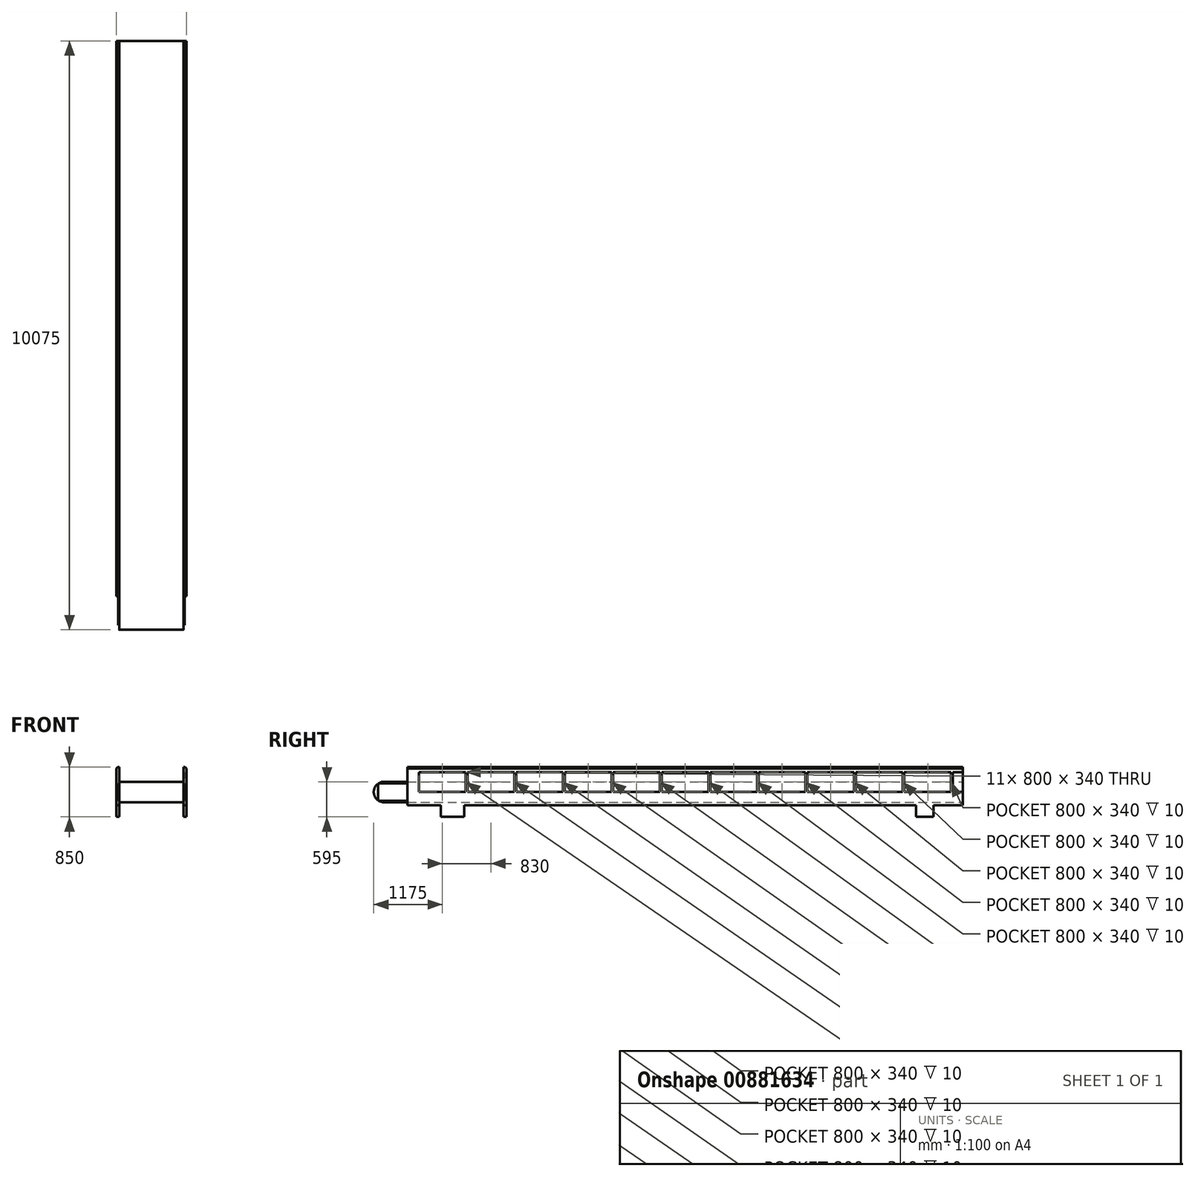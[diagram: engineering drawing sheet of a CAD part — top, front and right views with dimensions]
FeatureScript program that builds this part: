
annotation { "Feature Type Name" : "Feature", "Feature Type Description" : "" }
export const myFeature = defineFeature(function(context is Context, id is Id, definition is map)
    precondition{}
    {
        {
            var Q0;
            Q0=qCreatedBy(makeId("Right.planeOp"),FACE);
            cPlane(context, id + "F0", {"entities" : qUnion([Q0]), "cplaneType" : CPlaneType.OFFSET, "offset" : 550 * mm, "width" : 150 * mm, "height" : 150 * mm});
        }
        {
            var Q0;
            Q0=qCreatedBy(makeId("Right.planeOp"),FACE);
            var sketch = newSketch(context, id + "F1", { "sketchPlane" : qUnion([Q0])});
            skCircle(sketch, "E0", {"center": v(0, 0) * mm, "radius": 150 * mm});
            skCircle(sketch, "E1.1.0.0", {"center": v(12700, 0) * mm, "radius": 150 * mm});
            skLineSegment(sketch, "E1.direction1", {"start": v(0, 0) * mm, "end": v(12700, 0) * mm, "construction": true});
            skSolve(sketch);
        }
        {
            var Q0;
            Q0=qSketchRegion(id+"F1",true);
            var Q1;
            Q1=qConstructionFilter(qBodyType(qCreatedBy(id+"F1",EDGE),BodyType.WIRE),ConstructionObject.NO);
            extrude(context, id + "F2", {"entities" : qUnion([Q0]), "surfaceEntities" : qUnion([Q1]), "depth" : 1100 * mm, "offsetDistance" : 25 * mm});
        }
        {
            var Q0;
            Q0=makeQuery(id+"F2.opExtrude","CAP_FACE",FACE,{"disambiguationData":[OSD([sQuery(id+"F1.wireOp",EDGE,"E0")])],"isStart":false});
            var sketch = newSketch(context, id + "F3", { "sketchPlane" : qUnion([Q0])});
            skCircle(sketch, "E2", {"center": v(0, 0) * mm, "radius": 175 * mm});
            skCircle(sketch, "E3", {"center": v(12700, 0) * mm, "radius": 175 * mm});
            skLineSegment(sketch, "E4.bottom", {"start": v(0, 175) * mm, "end": v(12700, 175) * mm});
            skLineSegment(sketch, "E4.top", {"start": v(0, -175) * mm, "end": v(12700, -175) * mm});
            skLineSegment(sketch, "E4.left", {"start": v(0, 175) * mm, "end": v(0, -175) * mm});
            skLineSegment(sketch, "E4.right", {"start": v(12700, 175) * mm, "end": v(12700, -175) * mm});
            skSolve(sketch);
        }
        {
            var Q0;
            Q0=qSketchRegion(id+"F3",true);
            extrude(context, id + "F4", {"entities" : qUnion([Q0]), "oppositeDirection" : true, "depth" : 1100 * mm, "offsetDistance" : 25 * mm});
        }
        {
            var Q0;
            Q0=qCreatedBy(makeId("Front.planeOp"),FACE);
            var sketch = newSketch(context, id + "F5", { "sketchPlane" : qUnion([Q0])});
            skLineSegment(sketch, "E5.bottom", {"start": v(0, 425) * mm, "end": v(-25, 425) * mm});
            skLineSegment(sketch, "E5.top", {"start": v(0, -225) * mm, "end": v(-50, -225) * mm});
            skLineSegment(sketch, "E5.left", {"start": v(0, 425) * mm, "end": v(0, -225) * mm});
            skLineSegment(sketch, "E5.right", {"start": v(-50, 401.85) * mm, "end": v(-50, -225) * mm});
            skLineSegment(sketch, "E6", {"start": v(-25, 425) * mm, "end": v(-50, 401.85) * mm});
            skPoint(sketch, "E7.orphan", {"position": v(-50, 425) * mm});
            skLineSegment(sketch, "E8.MirrorCS", {"start": v(1100, 425) * mm, "end": v(1125, 425) * mm});
            skLineSegment(sketch, "E9.MirrorCS", {"start": v(1125, 425) * mm, "end": v(1150, 401.85) * mm});
            skLineSegment(sketch, "E10.MirrorCS", {"start": v(1100, -225) * mm, "end": v(1150, -225) * mm});
            skPoint(sketch, "E11.MirrorP", {"position": v(1150, 425) * mm});
            skLineSegment(sketch, "E12.MirrorCS", {"start": v(1150, 401.85) * mm, "end": v(1150, -225) * mm});
            skLineSegment(sketch, "E13.MirrorCS", {"start": v(1100, 425) * mm, "end": v(1100, -225) * mm});
            skSolve(sketch);
        }
        {
            var Q0;
            Q0=qSketchRegion(id+"F5",true);
            extrude(context, id + "F6", {"entities" : qUnion([Q0]), "oppositeDirection" : true, "depth" : 12400 * mm, "offsetDistance" : 25 * mm, "hasSecondDirection" : true, "secondDirectionOppositeDirection" : false, "secondDirectionDepth" : -400 * mm});
        }
        {
            var Q0;
            Q0=makeQuery(id+"F6.opExtrude","CAP_FACE",FACE,{"disambiguationData":[OSD([sQuery(id+"F5.wireOp",EDGE,"E5.bottom"),sQuery(id+"F5.wireOp",EDGE,"E5.top"),sQuery(id+"F5.wireOp",EDGE,"E5.left"),sQuery(id+"F5.wireOp",EDGE,"E5.right"),sQuery(id+"F5.wireOp",EDGE,"E6")])],"isStart":true});
            var sketch = newSketch(context, id + "F7", { "sketchPlane" : qUnion([Q0])});
            skLineSegment(sketch, "E14.bottom", {"start": v(0, 150) * mm, "end": v(-20, 150) * mm});
            skLineSegment(sketch, "E14.top", {"start": v(0, -150) * mm, "end": v(-20, -150) * mm});
            skLineSegment(sketch, "E14.left", {"start": v(0, 150) * mm, "end": v(0, -150) * mm});
            skLineSegment(sketch, "E14.right", {"start": v(-20, 150) * mm, "end": v(-20, -150) * mm});
            skLineSegment(sketch, "E15.MirrorCS", {"start": v(1100, -150) * mm, "end": v(1120, -150) * mm});
            skLineSegment(sketch, "E16.MirrorCS", {"start": v(1100, 150) * mm, "end": v(1120, 150) * mm});
            skLineSegment(sketch, "E17.MirrorCS", {"start": v(1120, 150) * mm, "end": v(1120, -150) * mm});
            skLineSegment(sketch, "E18.MirrorCS", {"start": v(1100, 150) * mm, "end": v(1100, -150) * mm});
            skSolve(sketch);
        }
        {
            var Q0;
            Q0=qSketchRegion(id+"F7",true);
            extrude(context, id + "F8", {"entities" : qUnion([Q0]), "operationType" : NewBodyOperationType.ADD, "depth" : 500 * mm, "offsetDistance" : 25 * mm, "hasSecondDirection" : true, "secondDirectionOppositeDirection" : true, "secondDirectionDepth" : 12500 * mm});
        }
        {
            var Q0;
            Q0=makeQuery(id+"F6.opExtrude","SWEPT_FACE",FACE,{"disambiguationData":[OSD([sQuery(id+"F5.wireOp",EDGE,"E5.right")])]});
            var sketch = newSketch(context, id + "F9", { "sketchPlane" : qUnion([Q0])});
            skLineSegment(sketch, "E19.bottom", {"start": v(-600, 340) * mm, "end": v(-1400, 340) * mm});
            skLineSegment(sketch, "E19.top", {"start": v(-600, 0) * mm, "end": v(-1400, 0) * mm});
            skLineSegment(sketch, "E19.left", {"start": v(-600, 340) * mm, "end": v(-600, 0) * mm});
            skLineSegment(sketch, "E19.right", {"start": v(-1400, 340) * mm, "end": v(-1400, 0) * mm});
            skLineSegment(sketch, "E20.1.0.0", {"start": v(-1430, 0) * mm, "end": v(-2230, 0) * mm});
            skLineSegment(sketch, "E20.1.0.1", {"start": v(-2230, 340) * mm, "end": v(-2230, 0) * mm});
            skLineSegment(sketch, "E20.1.0.2", {"start": v(-1430, 340) * mm, "end": v(-1430, 0) * mm});
            skLineSegment(sketch, "E20.1.0.3", {"start": v(-1430, 340) * mm, "end": v(-2230, 340) * mm});
            skLineSegment(sketch, "E20.2.0.0", {"start": v(-2260, 0) * mm, "end": v(-3060, 0) * mm});
            skLineSegment(sketch, "E20.2.0.1", {"start": v(-3060, 340) * mm, "end": v(-3060, 0) * mm});
            skLineSegment(sketch, "E20.2.0.2", {"start": v(-2260, 340) * mm, "end": v(-2260, 0) * mm});
            skLineSegment(sketch, "E20.2.0.3", {"start": v(-2260, 340) * mm, "end": v(-3060, 340) * mm});
            skLineSegment(sketch, "E20.3.0.0", {"start": v(-3090, 0) * mm, "end": v(-3890, 0) * mm});
            skLineSegment(sketch, "E20.3.0.1", {"start": v(-3890, 340) * mm, "end": v(-3890, 0) * mm});
            skLineSegment(sketch, "E20.3.0.2", {"start": v(-3090, 340) * mm, "end": v(-3090, 0) * mm});
            skLineSegment(sketch, "E20.3.0.3", {"start": v(-3090, 340) * mm, "end": v(-3890, 340) * mm});
            skLineSegment(sketch, "E20.4.0.0", {"start": v(-3920, 0) * mm, "end": v(-4720, 0) * mm});
            skLineSegment(sketch, "E20.4.0.1", {"start": v(-4720, 340) * mm, "end": v(-4720, 0) * mm});
            skLineSegment(sketch, "E20.4.0.2", {"start": v(-3920, 340) * mm, "end": v(-3920, 0) * mm});
            skLineSegment(sketch, "E20.4.0.3", {"start": v(-3920, 340) * mm, "end": v(-4720, 340) * mm});
            skLineSegment(sketch, "E20.5.0.0", {"start": v(-4750, 0) * mm, "end": v(-5550, 0) * mm});
            skLineSegment(sketch, "E20.5.0.1", {"start": v(-5550, 340) * mm, "end": v(-5550, 0) * mm});
            skLineSegment(sketch, "E20.5.0.2", {"start": v(-4750, 340) * mm, "end": v(-4750, 0) * mm});
            skLineSegment(sketch, "E20.5.0.3", {"start": v(-4750, 340) * mm, "end": v(-5550, 340) * mm});
            skLineSegment(sketch, "E20.6.0.0", {"start": v(-5580, 0) * mm, "end": v(-6380, 0) * mm});
            skLineSegment(sketch, "E20.6.0.1", {"start": v(-6380, 340) * mm, "end": v(-6380, 0) * mm});
            skLineSegment(sketch, "E20.6.0.2", {"start": v(-5580, 340) * mm, "end": v(-5580, 0) * mm});
            skLineSegment(sketch, "E20.6.0.3", {"start": v(-5580, 340) * mm, "end": v(-6380, 340) * mm});
            skLineSegment(sketch, "E20.7.0.0", {"start": v(-6410, 0) * mm, "end": v(-7210, 0) * mm});
            skLineSegment(sketch, "E20.7.0.1", {"start": v(-7210, 340) * mm, "end": v(-7210, 0) * mm});
            skLineSegment(sketch, "E20.7.0.2", {"start": v(-6410, 340) * mm, "end": v(-6410, 0) * mm});
            skLineSegment(sketch, "E20.7.0.3", {"start": v(-6410, 340) * mm, "end": v(-7210, 340) * mm});
            skLineSegment(sketch, "E20.8.0.0", {"start": v(-7240, 0) * mm, "end": v(-8040, 0) * mm});
            skLineSegment(sketch, "E20.8.0.1", {"start": v(-8040, 340) * mm, "end": v(-8040, 0) * mm});
            skLineSegment(sketch, "E20.8.0.2", {"start": v(-7240, 340) * mm, "end": v(-7240, 0) * mm});
            skLineSegment(sketch, "E20.8.0.3", {"start": v(-7240, 340) * mm, "end": v(-8040, 340) * mm});
            skLineSegment(sketch, "E20.9.0.0", {"start": v(-8070, 0) * mm, "end": v(-8870, 0) * mm});
            skLineSegment(sketch, "E20.9.0.1", {"start": v(-8870, 340) * mm, "end": v(-8870, 0) * mm});
            skLineSegment(sketch, "E20.9.0.2", {"start": v(-8070, 340) * mm, "end": v(-8070, 0) * mm});
            skLineSegment(sketch, "E20.9.0.3", {"start": v(-8070, 340) * mm, "end": v(-8870, 340) * mm});
            skLineSegment(sketch, "E20.10.0.0", {"start": v(-8900, 0) * mm, "end": v(-9700, 0) * mm});
            skLineSegment(sketch, "E20.10.0.1", {"start": v(-9700, 340) * mm, "end": v(-9700, 0) * mm});
            skLineSegment(sketch, "E20.10.0.2", {"start": v(-8900, 340) * mm, "end": v(-8900, 0) * mm});
            skLineSegment(sketch, "E20.10.0.3", {"start": v(-8900, 340) * mm, "end": v(-9700, 340) * mm});
            skLineSegment(sketch, "E20.11.0.0", {"start": v(-9730, 0) * mm, "end": v(-10530, 0) * mm});
            skLineSegment(sketch, "E20.11.0.1", {"start": v(-10530, 340) * mm, "end": v(-10530, 0) * mm});
            skLineSegment(sketch, "E20.11.0.2", {"start": v(-9730, 340) * mm, "end": v(-9730, 0) * mm});
            skLineSegment(sketch, "E20.11.0.3", {"start": v(-9730, 340) * mm, "end": v(-10530, 340) * mm});
            skLineSegment(sketch, "E20.12.0.0", {"start": v(-10560, 0) * mm, "end": v(-11360, 0) * mm});
            skLineSegment(sketch, "E20.12.0.1", {"start": v(-11360, 340) * mm, "end": v(-11360, 0) * mm});
            skLineSegment(sketch, "E20.12.0.2", {"start": v(-10560, 340) * mm, "end": v(-10560, 0) * mm});
            skLineSegment(sketch, "E20.12.0.3", {"start": v(-10560, 340) * mm, "end": v(-11360, 340) * mm});
            skLineSegment(sketch, "E20.13.0.0", {"start": v(-11390, 0) * mm, "end": v(-12190, 0) * mm});
            skLineSegment(sketch, "E20.13.0.1", {"start": v(-12190, 340) * mm, "end": v(-12190, 0) * mm});
            skLineSegment(sketch, "E20.13.0.2", {"start": v(-11390, 340) * mm, "end": v(-11390, 0) * mm});
            skLineSegment(sketch, "E20.13.0.3", {"start": v(-11390, 340) * mm, "end": v(-12190, 340) * mm});
            skLineSegment(sketch, "E20.direction1", {"start": v(-1400, 0) * mm, "end": v(-2230, 0) * mm, "construction": true});
            skSolve(sketch);
        }
        {
            var Q0;
            Q0=qSketchRegion(id+"F9",true);
            extrude(context, id + "F10", {"entities" : qUnion([Q0]), "operationType" : NewBodyOperationType.REMOVE, "oppositeDirection" : true, "depth" : 10 * mm, "offsetDistance" : 25 * mm});
        }
        {
            var Q0;
            Q0=makeQuery(id+"F6.opExtrude","SWEPT_FACE",FACE,{"disambiguationData":[OSD([sQuery(id+"F5.wireOp",EDGE,"E12.MirrorCS")])]});
            var sketch = newSketch(context, id + "F11", { "sketchPlane" : qUnion([Q0])});
            skLineSegment(sketch, "E21.0.0", {"start": v(1400, 0) * mm, "end": v(600, 0) * mm});
            skLineSegment(sketch, "E21.0.1", {"start": v(600, 0) * mm, "end": v(600, 340) * mm});
            skLineSegment(sketch, "E21.0.2", {"start": v(600, 340) * mm, "end": v(1400, 340) * mm});
            skLineSegment(sketch, "E21.0.3", {"start": v(1400, 340) * mm, "end": v(1400, 0) * mm});
            skLineSegment(sketch, "E22.0.0", {"start": v(1430, 0) * mm, "end": v(1430, 340) * mm});
            skLineSegment(sketch, "E22.0.1", {"start": v(1430, 340) * mm, "end": v(2230, 340) * mm});
            skLineSegment(sketch, "E22.0.2", {"start": v(2230, 340) * mm, "end": v(2230, 0) * mm});
            skLineSegment(sketch, "E22.0.3", {"start": v(2230, 0) * mm, "end": v(1430, 0) * mm});
            skLineSegment(sketch, "E23.0.0", {"start": v(2260, 0) * mm, "end": v(2260, 340) * mm});
            skLineSegment(sketch, "E23.0.1", {"start": v(2260, 340) * mm, "end": v(3060, 340) * mm});
            skLineSegment(sketch, "E23.0.2", {"start": v(3060, 340) * mm, "end": v(3060, 0) * mm});
            skLineSegment(sketch, "E23.0.3", {"start": v(3060, 0) * mm, "end": v(2260, 0) * mm});
            skLineSegment(sketch, "E24.0.0", {"start": v(3090, 0) * mm, "end": v(3090, 340) * mm});
            skLineSegment(sketch, "E24.0.1", {"start": v(3090, 340) * mm, "end": v(3890, 340) * mm});
            skLineSegment(sketch, "E24.0.2", {"start": v(3890, 340) * mm, "end": v(3890, 0) * mm});
            skLineSegment(sketch, "E24.0.3", {"start": v(3890, 0) * mm, "end": v(3090, 0) * mm});
            skLineSegment(sketch, "E25.0.0", {"start": v(3920, 0) * mm, "end": v(3920, 340) * mm});
            skLineSegment(sketch, "E25.0.1", {"start": v(3920, 340) * mm, "end": v(4720, 340) * mm});
            skLineSegment(sketch, "E25.0.2", {"start": v(4720, 340) * mm, "end": v(4720, 0) * mm});
            skLineSegment(sketch, "E25.0.3", {"start": v(4720, 0) * mm, "end": v(3920, 0) * mm});
            skLineSegment(sketch, "E26.0.0", {"start": v(4750, 0) * mm, "end": v(4750, 340) * mm});
            skLineSegment(sketch, "E26.0.1", {"start": v(4750, 340) * mm, "end": v(5550, 340) * mm});
            skLineSegment(sketch, "E26.0.2", {"start": v(5550, 340) * mm, "end": v(5550, 0) * mm});
            skLineSegment(sketch, "E26.0.3", {"start": v(5550, 0) * mm, "end": v(4750, 0) * mm});
            skLineSegment(sketch, "E27.0.0", {"start": v(5580, 0) * mm, "end": v(5580, 340) * mm});
            skLineSegment(sketch, "E27.0.1", {"start": v(5580, 340) * mm, "end": v(6380, 340) * mm});
            skLineSegment(sketch, "E27.0.2", {"start": v(6380, 340) * mm, "end": v(6380, 0) * mm});
            skLineSegment(sketch, "E27.0.3", {"start": v(6380, 0) * mm, "end": v(5580, 0) * mm});
            skLineSegment(sketch, "E28.0.0", {"start": v(6410, 0) * mm, "end": v(6410, 340) * mm});
            skLineSegment(sketch, "E28.0.1", {"start": v(6410, 340) * mm, "end": v(7210, 340) * mm});
            skLineSegment(sketch, "E28.0.2", {"start": v(7210, 340) * mm, "end": v(7210, 0) * mm});
            skLineSegment(sketch, "E28.0.3", {"start": v(7210, 0) * mm, "end": v(6410, 0) * mm});
            skLineSegment(sketch, "E29.0.0", {"start": v(7240, 0) * mm, "end": v(7240, 340) * mm});
            skLineSegment(sketch, "E29.0.1", {"start": v(7240, 340) * mm, "end": v(8040, 340) * mm});
            skLineSegment(sketch, "E29.0.2", {"start": v(8040, 340) * mm, "end": v(8040, 0) * mm});
            skLineSegment(sketch, "E29.0.3", {"start": v(8040, 0) * mm, "end": v(7240, 0) * mm});
            skLineSegment(sketch, "E30.0.0", {"start": v(8070, 0) * mm, "end": v(8070, 340) * mm});
            skLineSegment(sketch, "E30.0.1", {"start": v(8070, 340) * mm, "end": v(8870, 340) * mm});
            skLineSegment(sketch, "E30.0.2", {"start": v(8870, 340) * mm, "end": v(8870, 0) * mm});
            skLineSegment(sketch, "E30.0.3", {"start": v(8870, 0) * mm, "end": v(8070, 0) * mm});
            skLineSegment(sketch, "E31.0.0", {"start": v(8900, 0) * mm, "end": v(8900, 340) * mm});
            skLineSegment(sketch, "E31.0.1", {"start": v(8900, 340) * mm, "end": v(9700, 340) * mm});
            skLineSegment(sketch, "E31.0.2", {"start": v(9700, 340) * mm, "end": v(9700, 0) * mm});
            skLineSegment(sketch, "E31.0.3", {"start": v(9700, 0) * mm, "end": v(8900, 0) * mm});
            skLineSegment(sketch, "E32.0.0", {"start": v(9730, 0) * mm, "end": v(9730, 340) * mm});
            skLineSegment(sketch, "E32.0.1", {"start": v(9730, 340) * mm, "end": v(10530, 340) * mm});
            skLineSegment(sketch, "E32.0.2", {"start": v(10530, 340) * mm, "end": v(10530, 0) * mm});
            skLineSegment(sketch, "E32.0.3", {"start": v(10530, 0) * mm, "end": v(9730, 0) * mm});
            skLineSegment(sketch, "E33.0.0", {"start": v(10560, 0) * mm, "end": v(10560, 340) * mm});
            skLineSegment(sketch, "E33.0.1", {"start": v(10560, 340) * mm, "end": v(11360, 340) * mm});
            skLineSegment(sketch, "E33.0.2", {"start": v(11360, 340) * mm, "end": v(11360, 0) * mm});
            skLineSegment(sketch, "E33.0.3", {"start": v(11360, 0) * mm, "end": v(10560, 0) * mm});
            skLineSegment(sketch, "E34.0.0", {"start": v(11390, 0) * mm, "end": v(11390, 340) * mm});
            skLineSegment(sketch, "E34.0.1", {"start": v(11390, 340) * mm, "end": v(12190, 340) * mm});
            skLineSegment(sketch, "E34.0.2", {"start": v(12190, 340) * mm, "end": v(12190, 0) * mm});
            skLineSegment(sketch, "E34.0.3", {"start": v(12190, 0) * mm, "end": v(11390, 0) * mm});
            skSolve(sketch);
        }
        {
            var Q0;
            Q0=qSketchRegion(id+"F11",true);
            extrude(context, id + "F12", {"entities" : qUnion([Q0]), "operationType" : NewBodyOperationType.REMOVE, "oppositeDirection" : true, "depth" : 10 * mm, "offsetDistance" : 25 * mm});
        }
        {
            var Q0;
            Q0=makeQuery(id+"F6.opExtrude","SWEPT_FACE",FACE,{"disambiguationData":[OSD([sQuery(id+"F5.wireOp",EDGE,"E10.MirrorCS")])]});
            var sketch = newSketch(context, id + "F13", { "sketchPlane" : qUnion([Q0])});
            skLineSegment(sketch, "E35.bottom", {"start": v(1150, -971.53) * mm, "end": v(1100, -971.53) * mm});
            skLineSegment(sketch, "E35.top", {"start": v(1150, -1371.53) * mm, "end": v(1100, -1371.53) * mm});
            skLineSegment(sketch, "E35.left", {"start": v(1150, -971.53) * mm, "end": v(1150, -1371.53) * mm});
            skLineSegment(sketch, "E35.right", {"start": v(1100, -971.53) * mm, "end": v(1100, -1371.53) * mm});
            skLineSegment(sketch, "E36.0.1.0", {"start": v(1100, -11471.53) * mm, "end": v(1100, -11871.53) * mm});
            skLineSegment(sketch, "E36.0.1.1", {"start": v(1150, -11471.53) * mm, "end": v(1100, -11471.53) * mm});
            skLineSegment(sketch, "E36.0.1.2", {"start": v(1150, -11871.53) * mm, "end": v(1100, -11871.53) * mm});
            skLineSegment(sketch, "E36.0.1.3", {"start": v(1150, -11471.53) * mm, "end": v(1150, -11871.53) * mm});
            skLineSegment(sketch, "E36.1.0.0", {"start": v(-50, -971.53) * mm, "end": v(-50, -1371.53) * mm});
            skLineSegment(sketch, "E36.1.0.1", {"start": v(0, -971.53) * mm, "end": v(-50, -971.53) * mm});
            skLineSegment(sketch, "E36.1.0.2", {"start": v(0, -1371.53) * mm, "end": v(-50, -1371.53) * mm});
            skLineSegment(sketch, "E36.1.0.3", {"start": v(0, -971.53) * mm, "end": v(0, -1371.53) * mm});
            skLineSegment(sketch, "E36.1.1.0", {"start": v(-50, -11471.53) * mm, "end": v(-50, -11871.53) * mm});
            skLineSegment(sketch, "E36.1.1.1", {"start": v(0, -11471.53) * mm, "end": v(-50, -11471.53) * mm});
            skLineSegment(sketch, "E36.1.1.2", {"start": v(0, -11871.53) * mm, "end": v(-50, -11871.53) * mm});
            skLineSegment(sketch, "E36.1.1.3", {"start": v(0, -11471.53) * mm, "end": v(0, -11871.53) * mm});
            skLineSegment(sketch, "E36.direction1", {"start": v(1100, -1371.53) * mm, "end": v(-50, -1371.53) * mm, "construction": true});
            skLineSegment(sketch, "E36.direction2", {"start": v(1100, -1371.53) * mm, "end": v(1100, -11871.53) * mm, "construction": true});
            skSolve(sketch);
        }
        {
            var Q0;
            Q0=qSketchRegion(id+"F13",true);
            extrude(context, id + "F14", {"entities" : qUnion([Q0]), "operationType" : NewBodyOperationType.ADD, "depth" : 200 * mm, "offsetDistance" : 25 * mm});
        }
        {
            var Q0;
            Q0=makeQuery(id+"F8.opExtrude","CAP_FACE",FACE,{"disambiguationData":[OSD([sQuery(id+"F7.wireOp",EDGE,"E15.MirrorCS"),sQuery(id+"F7.wireOp",EDGE,"E16.MirrorCS"),sQuery(id+"F7.wireOp",EDGE,"E17.MirrorCS"),sQuery(id+"F7.wireOp",EDGE,"E18.MirrorCS")])],"isStart":true});
            var sketch = newSketch(context, id + "F15", { "sketchPlane" : qUnion([Q0])});
            skLineSegment(sketch, "E37.bottom", {"start": v(-1475.5, 594.26) * mm, "end": v(339.13, 594.26) * mm});
            skLineSegment(sketch, "E37.top", {"start": v(-1475.5, -532.92) * mm, "end": v(339.13, -532.92) * mm});
            skLineSegment(sketch, "E37.left", {"start": v(-1475.5, 594.26) * mm, "end": v(-1475.5, -532.92) * mm});
            skLineSegment(sketch, "E37.right", {"start": v(339.13, 594.26) * mm, "end": v(339.13, -532.92) * mm});
            skSolve(sketch);
        }
        {
            var Q0;
            Q0 = qSketchRegion(id + "F15", true);
            extrude(context, id + "F16", {"entities" : qUnion([Q0]), "operationType" : NewBodyOperationType.REMOVE, "oppositeDirection" : true, "depth" : 3000 * mm, "offsetDistance" : 25 * mm});
        }
        {
            var Q0;
            Q0=makeQuery(id+"F14.boolean.opBoolean","SPLIT",FACE,{"disambiguationData":[TD([makeQuery(id+"F14.opExtrude","SWEPT_FACE",FACE,{"disambiguationData":[OSD([sQuery(id+"F13.wireOp",EDGE,"E35.top")])]})])],"derivedFrom":makeQuery(id+"F6.opExtrude","SWEPT_FACE",FACE,{"disambiguationData":[OSD([sQuery(id+"F5.wireOp",EDGE,"E10.MirrorCS")])]})});
            var sketch = newSketch(context, id + "F17", { "sketchPlane" : qUnion([Q0])});
            skLineSegment(sketch, "E38.bottom", {"start": v(1150, -9100) * mm, "end": v(1100, -9100) * mm});
            skLineSegment(sketch, "E38.top", {"start": v(1150, -9400) * mm, "end": v(1100, -9400) * mm});
            skLineSegment(sketch, "E38.left", {"start": v(1150, -9100) * mm, "end": v(1150, -9400) * mm});
            skLineSegment(sketch, "E38.right", {"start": v(1100, -9100) * mm, "end": v(1100, -9400) * mm});
            skLineSegment(sketch, "E39.bottom", {"start": v(0, -9100) * mm, "end": v(-50, -9100) * mm});
            skLineSegment(sketch, "E39.top", {"start": v(0, -9400) * mm, "end": v(-50, -9400) * mm});
            skLineSegment(sketch, "E39.left", {"start": v(0, -9100) * mm, "end": v(0, -9400) * mm});
            skLineSegment(sketch, "E39.right", {"start": v(-50, -9100) * mm, "end": v(-50, -9400) * mm});
            skSolve(sketch);
        }
        {
            var Q0;
            Q0 = qSketchRegion(id + "F17", true);
            extrude(context, id + "F18", {"entities" : qUnion([Q0]), "operationType" : NewBodyOperationType.ADD, "depth" : 200 * mm, "offsetDistance" : 25 * mm});
        }
    });
